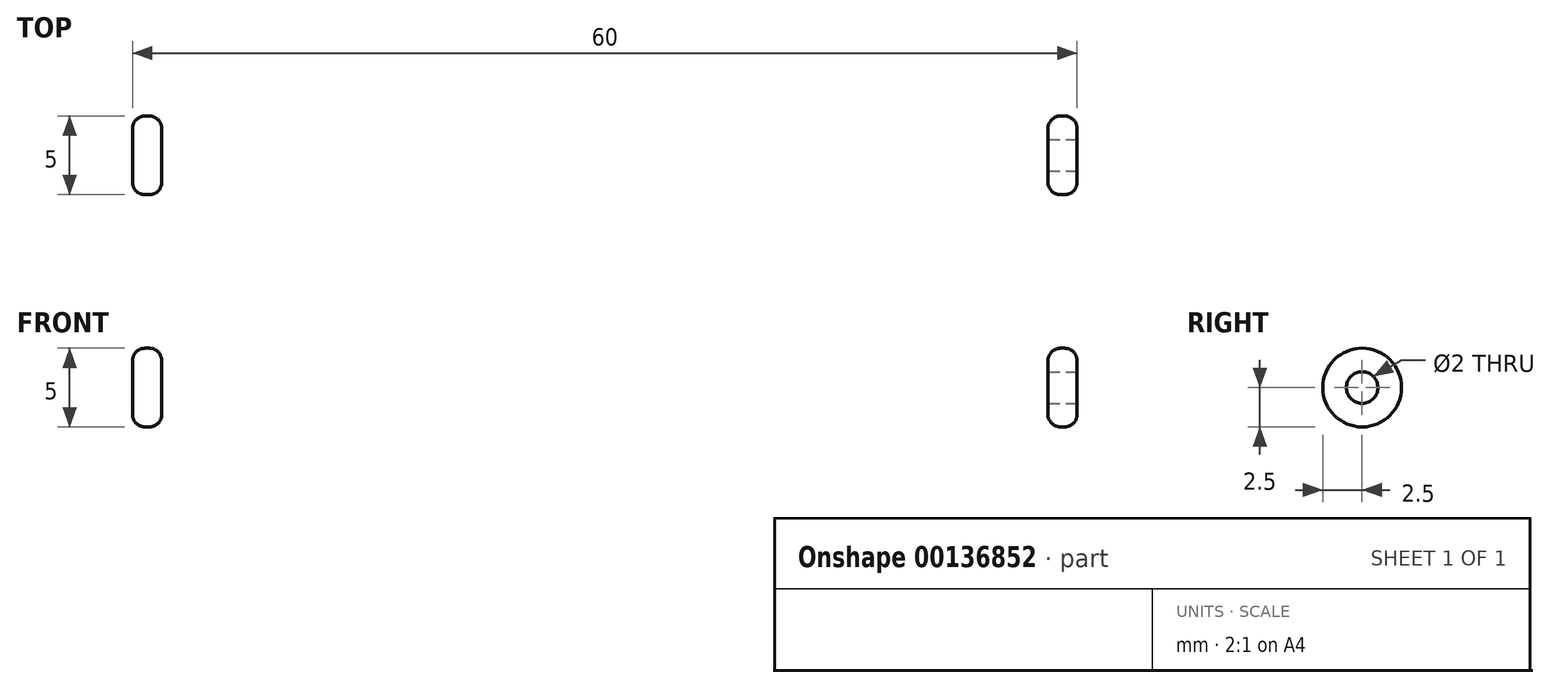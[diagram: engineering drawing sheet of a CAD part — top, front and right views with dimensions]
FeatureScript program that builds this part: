
annotation { "Feature Type Name" : "Feature", "Feature Type Description" : "" }
export const myFeature = defineFeature(function(context is Context, id is Id, definition is map)
    precondition{}
    {
        {
            var Q0;
            Q0=qCreatedBy(makeId("Front.planeOp"),FACE);
            var sketch = newSketch(context, id + "F0", { "sketchPlane" : qUnion([Q0])});
            skLineSegment(sketch, "E0", {"start": v(0, 0) * mm, "end": v(30, 0) * mm});
            skLineSegment(sketch, "E1", {"start": v(30, 0) * mm, "end": v(-30, 0) * mm});
            skLineSegment(sketch, "E2", {"start": v(-30, 0) * mm, "end": v(-30, 2.5) * mm});
            skLineSegment(sketch, "E3", {"start": v(-30, 2.5) * mm, "end": v(-30, -2.5) * mm});
            skLineSegment(sketch, "E4", {"start": v(-30, -2.5) * mm, "end": v(-28.14, -2.5) * mm});
            skLineSegment(sketch, "E5", {"start": v(-28.14, -2.5) * mm, "end": v(-28.14, 2.5) * mm});
            skLineSegment(sketch, "E6", {"start": v(-28.14, 2.5) * mm, "end": v(-30, 2.5) * mm});
            skLineSegment(sketch, "E7", {"start": v(30, 0) * mm, "end": v(30, 2.5) * mm});
            skLineSegment(sketch, "E8", {"start": v(30, 2.5) * mm, "end": v(30, -2.5) * mm});
            skLineSegment(sketch, "E9", {"start": v(30, -2.5) * mm, "end": v(28.14, -2.5) * mm});
            skLineSegment(sketch, "E10", {"start": v(28.14, -2.5) * mm, "end": v(28.14, 2.5) * mm});
            skLineSegment(sketch, "E11", {"start": v(28.14, 2.5) * mm, "end": v(30, 2.5) * mm});
            skLineSegment(sketch, "E12", {"start": v(-30, 0) * mm, "end": v(-30, 1) * mm});
            skLineSegment(sketch, "E13", {"start": v(-30, 0) * mm, "end": v(-30, -1) * mm});
            skLineSegment(sketch, "E14", {"start": v(-30, -1) * mm, "end": v(30, -1) * mm});
            skLineSegment(sketch, "E15", {"start": v(30, -1) * mm, "end": v(30, 1) * mm});
            skLineSegment(sketch, "E16", {"start": v(30, 1) * mm, "end": v(-30, 1) * mm});
            skSolve(sketch);
        }
        {
            var Q0;
            {var subQ0=sQuery(id+"F0.wireOp",EDGE,"E12");Q0=makeQuery(id+"F0.imprint","IMPRINT",FACE,{"disambiguationData":[TD([[makeQuery(id+"F0.imprint","IMPRINT",EDGE,{"derivedFrom":subQ0}),-1.0]])]});}
            var Q1;
            {var subQ3=sQuery(id+"F0.wireOp",EDGE,"E1");var subQ5=makeQuery(id+"F0.imprint","IMPRINT",VERTEX,{"derivedFrom":subQ3});Q1=makeQuery(id+"F0.imprint","IMPRINT",FACE,{"disambiguationData":[TD([[makeQuery(id+"F0.imprint","IMPRINT",EDGE,{"disambiguationData":[TD([[subQ5,1.0]])],"derivedFrom":subQ3}),-1.0]])]});}
            var Q2;
            {var subQ0=sQuery(id+"F0.wireOp",EDGE,"E15");var subQ1=sQuery(id+"F0.wireOp",EDGE,"E1");var subQ2=makeQuery(id+"F0.imprint","INTERSECT",VERTEX,{"derivedFrom":[subQ1,subQ0]});Q2=makeQuery(id+"F0.imprint","IMPRINT",FACE,{"disambiguationData":[TD([[makeQuery(id+"F0.imprint","IMPRINT",EDGE,{"disambiguationData":[TD([[subQ2,-1.0]])],"derivedFrom":subQ1}),-1.0]])]});}
            var Q3;
            {var subQ0=sQuery(id+"F0.wireOp",EDGE,"E11");Q3=makeQuery(id+"F0.imprint","IMPRINT",FACE,{"disambiguationData":[TD([[makeQuery(id+"F0.imprint","IMPRINT",EDGE,{"derivedFrom":subQ0}),-1.0]])]});}
            var Q4;
            {var subQ0=sQuery(id+"F0.wireOp",EDGE,"E6");Q4=makeQuery(id+"F0.imprint","IMPRINT",FACE,{"disambiguationData":[TD([[makeQuery(id+"F0.imprint","IMPRINT",EDGE,{"derivedFrom":subQ0}),1.0]])]});}
            var Q5;
            Q5=sQuery(id+"F0.wireOp",EDGE,"E1");
            revolve(context, id + "F1", {"entities" : qUnion([Q0, Q1, Q2, Q3, Q4]), "axis" : qUnion([Q5]), "revolveType" : RevolveType.FULL});
        }
        {
            var Q0;
            Q0=makeQuery(id+"F1.opRevolve","SWEPT_EDGE",EDGE,{"disambiguationData":[OSD([sQuery(id+"F0.wireOp",EDGE,"E3"),sQuery(id+"F0.wireOp",EDGE,"E6")])]});
            var Q1;
            Q1=makeQuery(id+"F1.opRevolve","SWEPT_EDGE",EDGE,{"disambiguationData":[OSD([sQuery(id+"F0.wireOp",EDGE,"E8"),sQuery(id+"F0.wireOp",EDGE,"E11")])]});
            fillet(context, id + "F2", {"entities" : qUnion([Q0, Q1]), "radius" : 0.8 * mm, "tangentPropagation" : true, "allowEdgeOverflow" : false});
        }
    });
